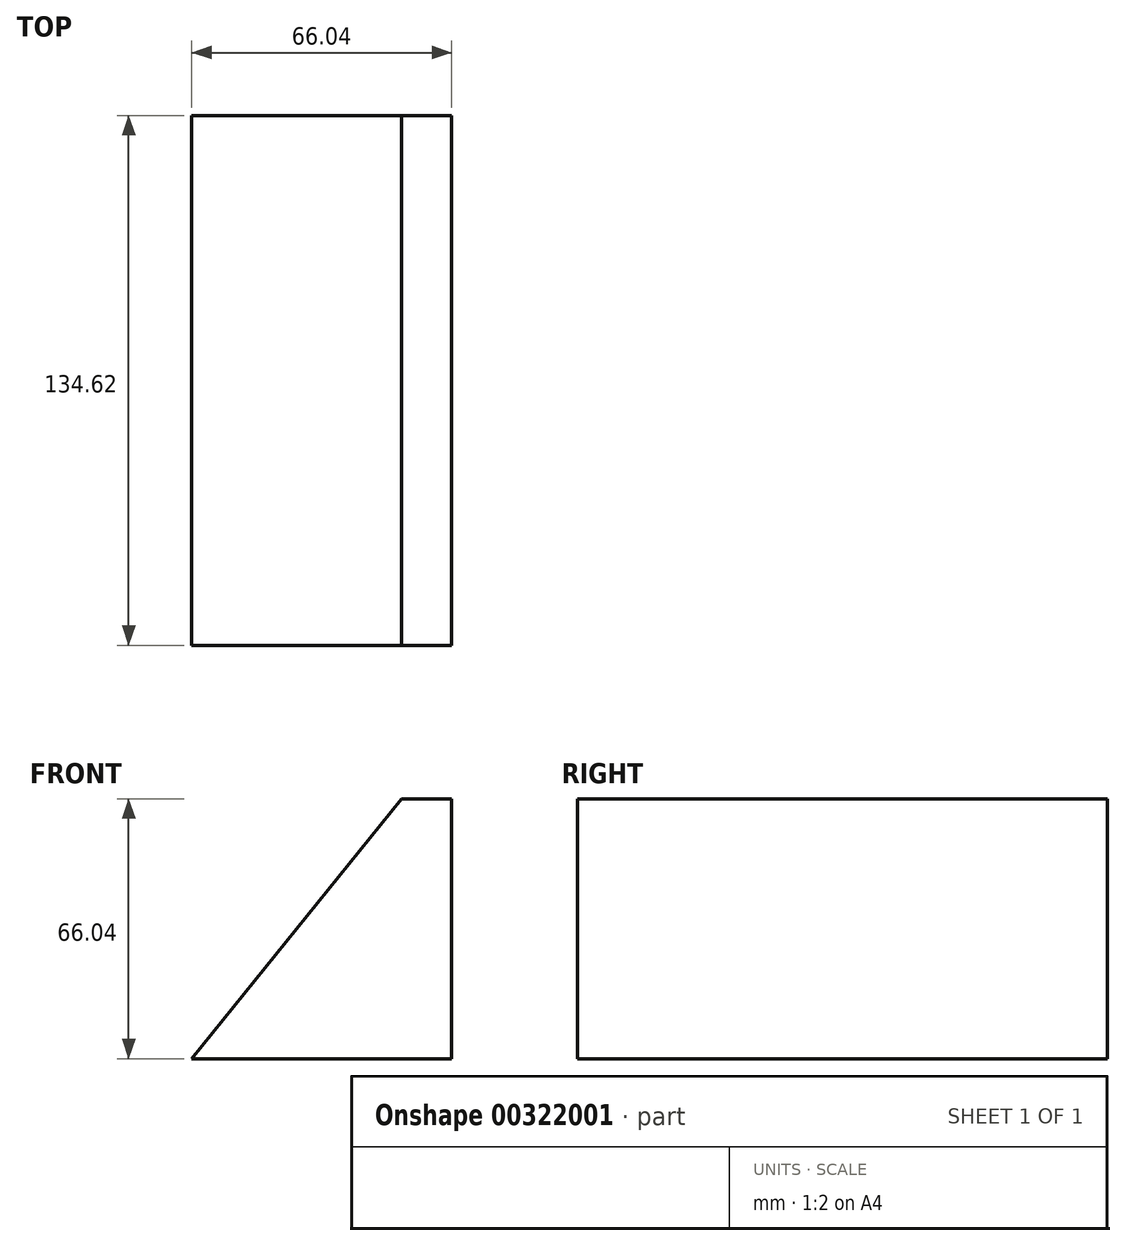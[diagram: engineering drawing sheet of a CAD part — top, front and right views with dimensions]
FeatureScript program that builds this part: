
annotation { "Feature Type Name" : "Feature", "Feature Type Description" : "" }
export const myFeature = defineFeature(function(context is Context, id is Id, definition is map)
    precondition{}
    {
        {
            var Q0;
            Q0=qCreatedBy(makeId("Front.planeOp"),FACE);
            var sketch = newSketch(context, id + "F0", { "sketchPlane" : qUnion([Q0])});
            skLineSegment(sketch, "E0", {"start": v(-1.93, 36.85) * mm, "end": v(10.77, 36.85) * mm});
            skLineSegment(sketch, "E1", {"start": v(10.77, 36.85) * mm, "end": v(10.77, -29.19) * mm});
            skLineSegment(sketch, "E2", {"start": v(10.77, -29.19) * mm, "end": v(-55.27, -29.19) * mm});
            skLineSegment(sketch, "E3", {"start": v(-55.27, -29.19) * mm, "end": v(-1.93, 36.85) * mm});
            skSolve(sketch);
        }
        {
            var Q0;
            Q0=makeQuery(id+"F0.imprint","IMPRINT",FACE,{"disambiguationData":[TD([[makeQuery(id+"F0.imprint","IMPRINT",EDGE,{"derivedFrom":sQuery(id+"F0.wireOp",EDGE,"E0")}),-1.0]])]});
            extrude(context, id + "F1", {"entities" : qUnion([Q0]), "endBound" : BoundingType.SYMMETRIC, "depth" : 134.62 * mm});
        }
    });
